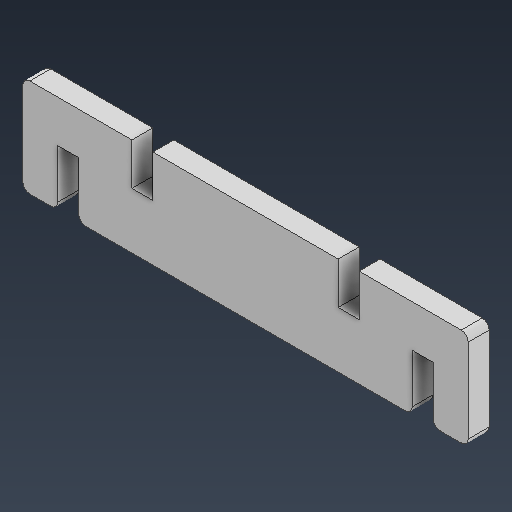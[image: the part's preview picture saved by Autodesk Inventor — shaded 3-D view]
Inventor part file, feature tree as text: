
AUTODESK INVENTOR PART (.ipt)
format: ipt  version: 2025.3 (Build 293356000, 356)  size: 133,632 bytes
history: native  units: mm
features: other x1, extrude x1, sketch x1
ambient origin geometry x8: Origin, YZ Plane, XZ Plane, XY Plane, X Axis, Y Axis, Z Axis, Center Point
bodies: Body1 (feature_tree)
feature tree (3):
  other  "實體1"
  extrude  "擠出1"  Depth=10.0mm
  sketch  "草圖1"
